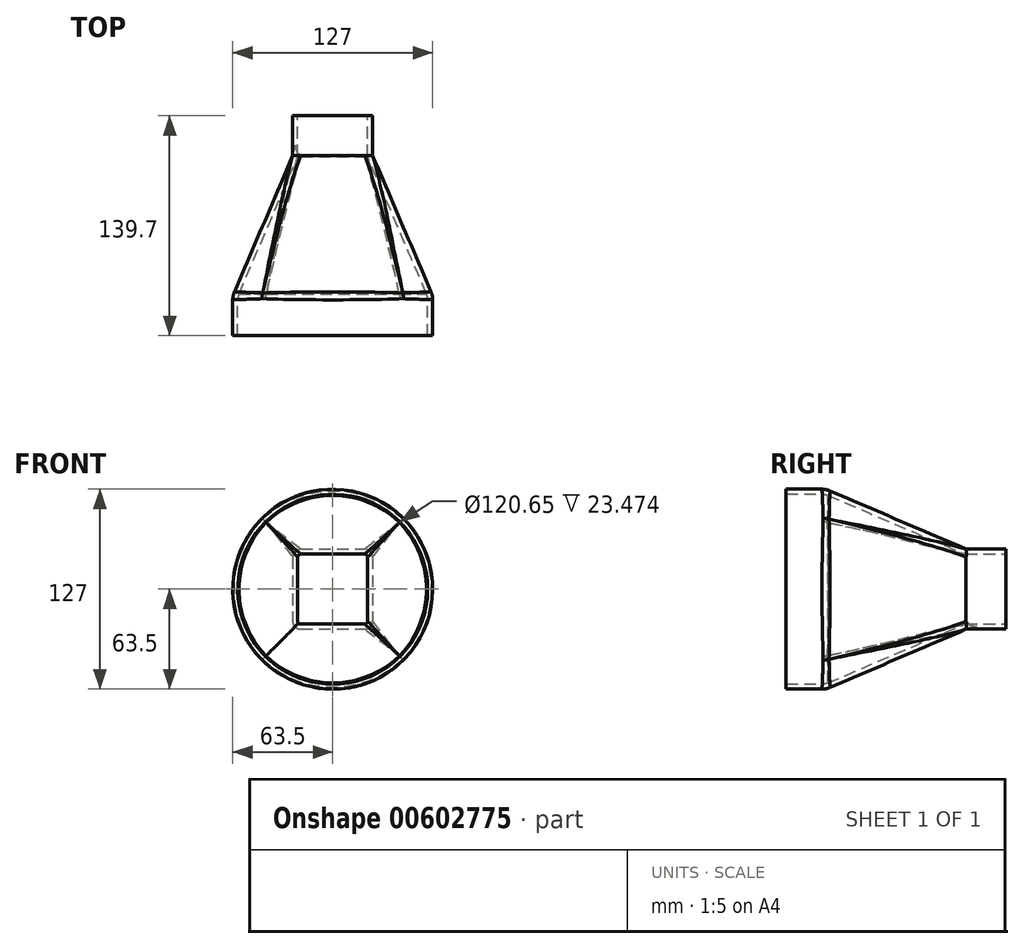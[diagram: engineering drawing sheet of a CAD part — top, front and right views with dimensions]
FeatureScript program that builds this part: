
annotation { "Feature Type Name" : "Feature", "Feature Type Description" : "" }
export const myFeature = defineFeature(function(context is Context, id is Id, definition is map)
    precondition{}
    {
        {
            var Q0;
            Q0=qCreatedBy(makeId("Front.planeOp"),FACE);
            var sketch = newSketch(context, id + "F0", { "sketchPlane" : qUnion([Q0])});
            skLineSegment(sketch, "E0.bottom", {"start": v(-25.4, 25.4) * mm, "end": v(25.4, 25.4) * mm});
            skLineSegment(sketch, "E0.top", {"start": v(-25.4, -25.4) * mm, "end": v(25.4, -25.4) * mm});
            skLineSegment(sketch, "E0.left", {"start": v(-25.4, 25.4) * mm, "end": v(-25.4, -25.4) * mm});
            skLineSegment(sketch, "E0.right", {"start": v(25.4, 25.4) * mm, "end": v(25.4, -25.4) * mm});
            skSolve(sketch);
        }
        {
            var Q0;
            Q0=makeQuery(id+"F0.imprint","IMPRINT",FACE,{"disambiguationData":[TD([[makeQuery(id+"F0.imprint","IMPRINT",EDGE,{"derivedFrom":sQuery(id+"F0.wireOp",EDGE,"E0.bottom")}),-1.0]])]});
            extrude(context, id + "F1", {"entities" : qUnion([Q0]), "flatOperationType" : FlatOperationType.REMOVE, "depth" : 25.4 * mm, "offsetDistance" : 25.4 * mm, "domain" : OperationDomain.MODEL, "symmetric" : true});
        }
        {
            var Q0;
            Q0=qCreatedBy(makeId("Front.planeOp"),FACE);
            cPlane(context, id + "F2", {"entities" : qUnion([Q0]), "cplaneType" : CPlaneType.OFFSET, "offset" : 101.6 * mm, "width" : 152.4 * mm, "height" : 152.4 * mm});
        }
        {
            var Q0;
            Q0=qCreatedBy(id+"F2.planeOp",FACE);
            var sketch = newSketch(context, id + "F3", { "sketchPlane" : qUnion([Q0])});
            skCircle(sketch, "E1", {"center": v(0, 0) * mm, "radius": 63.5 * mm});
            skSolve(sketch);
        }
        {
            var Q0;
            Q0 = qSketchRegion(id + "F3", true);
            extrude(context, id + "F4", {"entities" : qUnion([Q0]), "flatOperationType" : FlatOperationType.REMOVE, "depth" : 25.4 * mm, "offsetDistance" : 25.4 * mm, "domain" : OperationDomain.MODEL});
        }
        {
            var Q2;
            Q2=makeQuery(id+"F1.opExtrude","CAP_FACE",FACE,{"disambiguationData":[OSD([sQuery(id+"F0.wireOp",EDGE,"E0.bottom"),sQuery(id+"F0.wireOp",EDGE,"E0.top"),sQuery(id+"F0.wireOp",EDGE,"E0.left"),sQuery(id+"F0.wireOp",EDGE,"E0.right")])],"isStart":false});
            var Q3;
            Q3=makeQuery(id+"F4.opExtrude","CAP_FACE",FACE,{"disambiguationData":[OSD([sQuery(id+"F3.wireOp",EDGE,"E1")])],"isStart":true});
            loft(context, id + "F5", {"operationType" : NewBodyOperationType.ADD, "sheetProfilesArray" : [{ "sheetProfileEntities" : qUnion([Q2]) }, { "sheetProfileEntities" : qUnion([Q3]) }], "trimGuidesByProfiles" : true});
        }
        {
            var Q0;
            Q0=makeQuery(id+"F5.opLoft","SWEPT_EDGE",EDGE,{"disambiguationData":[OSD([sQuery(id+"F0.wireOp",EDGE,"E0.bottom"),sQuery(id+"F0.wireOp",EDGE,"E0.left")])]});
            var Q1;
            Q1=makeQuery(id+"F1.opExtrude","SWEPT_EDGE",EDGE,{"disambiguationData":[OSD([sQuery(id+"F0.wireOp",EDGE,"E0.bottom"),sQuery(id+"F0.wireOp",EDGE,"E0.left")])]});
            var Q2;
            Q2=makeQuery(id+"F5.opLoft","SWEPT_EDGE",EDGE,{"disambiguationData":[OSD([sQuery(id+"F0.wireOp",EDGE,"E0.bottom"),sQuery(id+"F0.wireOp",EDGE,"E0.top"),sQuery(id+"F0.wireOp",EDGE,"E0.left"),sQuery(id+"F3.wireOp",EDGE,"E1")])]});
            var Q3;
            Q3=makeQuery(id+"F1.opExtrude","SWEPT_EDGE",EDGE,{"disambiguationData":[OSD([sQuery(id+"F0.wireOp",EDGE,"E0.top"),sQuery(id+"F0.wireOp",EDGE,"E0.left")])]});
            var Q4;
            Q4=makeQuery(id+"F5.opLoft","SWEPT_EDGE",EDGE,{"disambiguationData":[OSD([sQuery(id+"F0.wireOp",EDGE,"E0.bottom"),sQuery(id+"F0.wireOp",EDGE,"E0.top"),sQuery(id+"F0.wireOp",EDGE,"E0.right"),sQuery(id+"F3.wireOp",EDGE,"E1")])]});
            var Q5;
            Q5=makeQuery(id+"F1.opExtrude","SWEPT_EDGE",EDGE,{"disambiguationData":[OSD([sQuery(id+"F0.wireOp",EDGE,"E0.bottom"),sQuery(id+"F0.wireOp",EDGE,"E0.right")])]});
            var Q6;
            Q6=makeQuery(id+"F5.opLoft","SWEPT_EDGE",EDGE,{"disambiguationData":[OSD([sQuery(id+"F0.wireOp",EDGE,"E0.top"),sQuery(id+"F0.wireOp",EDGE,"E0.left"),sQuery(id+"F0.wireOp",EDGE,"E0.right"),sQuery(id+"F3.wireOp",EDGE,"E1")])]});
            var Q7;
            Q7=makeQuery(id+"F1.opExtrude","SWEPT_EDGE",EDGE,{"disambiguationData":[OSD([sQuery(id+"F0.wireOp",EDGE,"E0.top"),sQuery(id+"F0.wireOp",EDGE,"E0.right")])]});
            fillet(context, id + "F6", {"entities" : qUnion([Q0, Q1, Q2, Q3, Q4, Q5, Q6, Q7]), "radius" : 5.08 * mm, "tangentPropagation" : true, "defaultsChanged" : false, "allowEdgeOverflow" : false, "vertexSettings" : []});
        }
        {
            var Q0;
            {var subQ0=sQuery(id+"F3.wireOp",EDGE,"E1");Q0=makeQuery(id+"F5.boolean.opBoolean","MERGE",EDGE,{"derivedFrom":[makeQuery(id+"F4.opExtrude","CAP_EDGE",EDGE,{"disambiguationData":[OSD([subQ0])],"isStart":true}),makeQuery(id+"F5.opLoft","MID_CAP_EDGE",EDGE,{"disambiguationData":[OSD([sQuery(id+"F0.wireOp",EDGE,"E0.bottom"),sQuery(id+"F0.wireOp",EDGE,"E0.top"),sQuery(id+"F0.wireOp",EDGE,"E0.left"),subQ0])],"capPos":1.0})]});}
            fillet(context, id + "F7", {"entities" : qUnion([Q0]), "radius" : 12.7 * mm, "tangentPropagation" : true, "defaultsChanged" : false, "allowEdgeOverflow" : false, "vertexSettings" : []});
        }
        {
            var Q0;
            Q0=makeQuery(id+"F4.opExtrude","CAP_FACE",FACE,{"disambiguationData":[OSD([sQuery(id+"F3.wireOp",EDGE,"E1")])],"isStart":false});
            var Q1;
            Q1=makeQuery(id+"F1.opExtrude","CAP_FACE",FACE,{"disambiguationData":[OSD([sQuery(id+"F0.wireOp",EDGE,"E0.bottom"),sQuery(id+"F0.wireOp",EDGE,"E0.top"),sQuery(id+"F0.wireOp",EDGE,"E0.left"),sQuery(id+"F0.wireOp",EDGE,"E0.right")])],"isStart":true});
            shell(context, id + "F8", {"entities" : qUnion([Q0, Q1]), "thickness" : 3.17 * mm});
        }
    });
